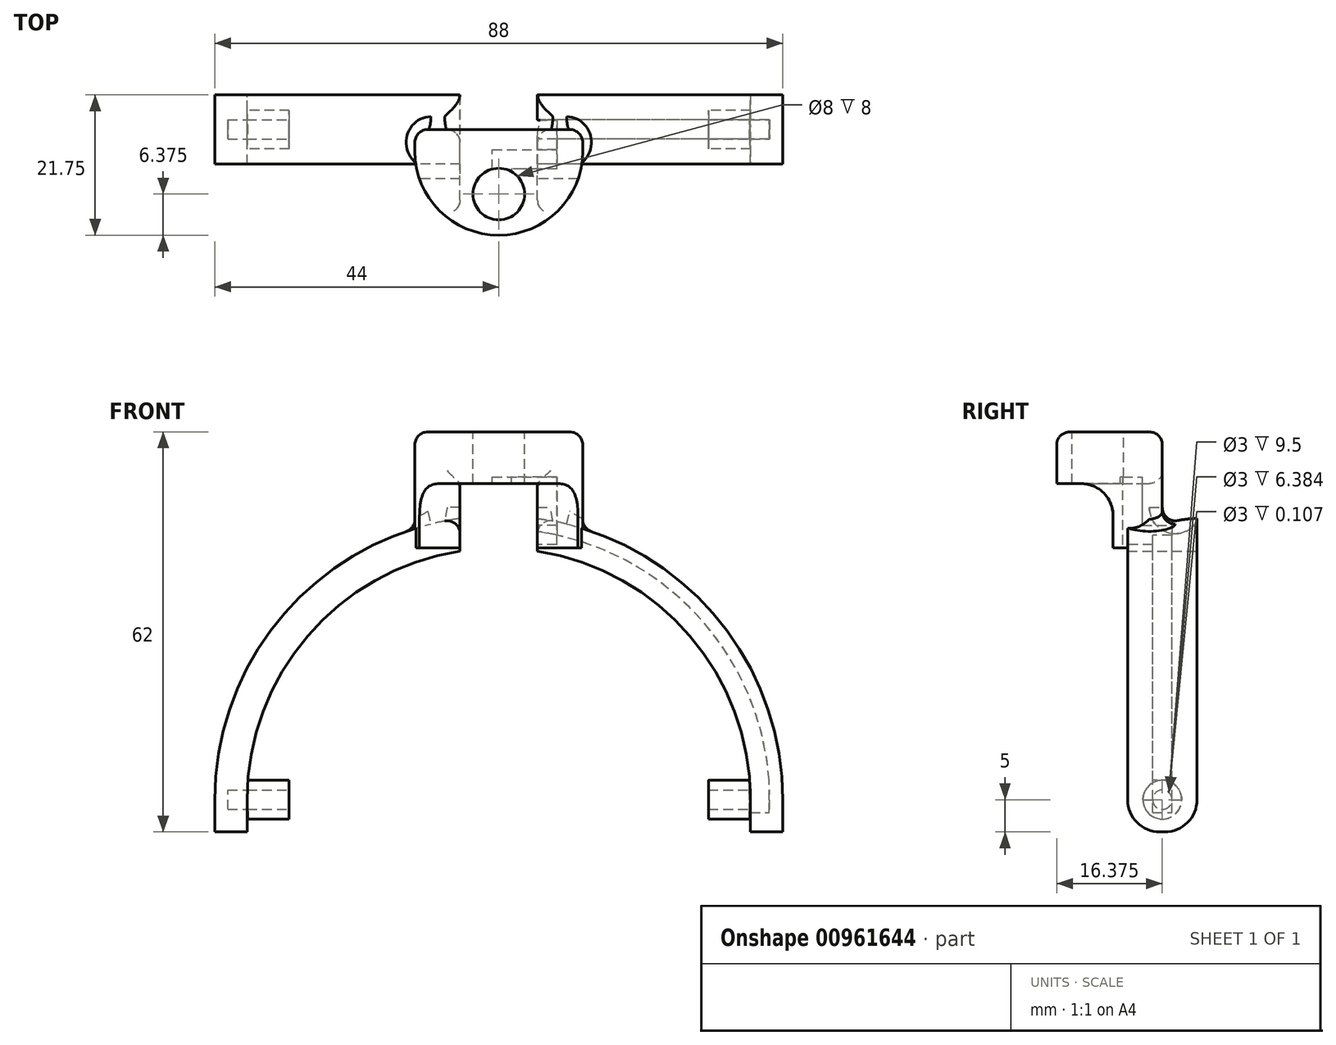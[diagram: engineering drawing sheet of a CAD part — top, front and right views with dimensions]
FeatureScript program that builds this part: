
annotation { "Feature Type Name" : "Feature", "Feature Type Description" : "" }
export const myFeature = defineFeature(function(context is Context, id is Id, definition is map)
    precondition{}
    {
        {
            var Q0;
            Q0=qCreatedBy(makeId("Front.planeOp"),FACE);
            var sketch = newSketch(context, id + "F0", { "sketchPlane" : qUnion([Q0])});
            skArc(sketch, "E0", {"start": v(39, 0) * mm, "mid": v(0, 39) * mm, "end": v(-39, 0) * mm});
            skArc(sketch, "E1", {"start": v(44, 0) * mm, "mid": v(0, 44) * mm, "end": v(-44, 0) * mm});
            skLineSegment(sketch, "E2", {"start": v(-44, 0) * mm, "end": v(-39, 0) * mm});
            skLineSegment(sketch, "E3", {"start": v(39, 0) * mm, "end": v(44, 0) * mm});
            skLineSegment(sketch, "E4", {"start": v(63.06, -5) * mm, "end": v(-58.13, -5) * mm, "construction": true});
            skLineSegment(sketch, "E5", {"start": v(44, 0) * mm, "end": v(44, -5) * mm});
            skLineSegment(sketch, "E6", {"start": v(44, -5) * mm, "end": v(39, -5) * mm});
            skLineSegment(sketch, "E7", {"start": v(39, -5) * mm, "end": v(39, 0) * mm});
            skLineSegment(sketch, "E8", {"start": v(-39, 0) * mm, "end": v(-39, -5) * mm});
            skLineSegment(sketch, "E9", {"start": v(-39, -5) * mm, "end": v(-44, -5) * mm});
            skLineSegment(sketch, "E10", {"start": v(-44, -5) * mm, "end": v(-44, 0) * mm});
            skSolve(sketch);
        }
        {
            var Q0;
            Q0=makeQuery(id+"F0.imprint","IMPRINT",FACE,{"disambiguationData":[TD([[makeQuery(id+"F0.imprint","IMPRINT",EDGE,{"derivedFrom":sQuery(id+"F0.wireOp",EDGE,"E0")}),-1.0]])]});
            var Q1;
            Q1=makeQuery(id+"F0.imprint","IMPRINT",FACE,{"disambiguationData":[TD([[makeQuery(id+"F0.imprint","IMPRINT",EDGE,{"derivedFrom":sQuery(id+"F0.wireOp",EDGE,"E3")}),-1.0]])]});
            var Q2;
            Q2=makeQuery(id+"F0.imprint","IMPRINT",FACE,{"disambiguationData":[TD([[makeQuery(id+"F0.imprint","IMPRINT",EDGE,{"derivedFrom":sQuery(id+"F0.wireOp",EDGE,"E2")}),-1.0]])]});
            extrude(context, id + "F1", {"entities" : qUnion([Q0, Q1, Q2]), "depth" : 10.75 * mm, "offsetDistance" : 25 * mm});
        }
        {
            var Q0;
            Q0=makeQuery(id+"F1.opExtrude","CAP_FACE",FACE,{"disambiguationData":[OSD([sQuery(id+"F0.wireOp",EDGE,"E0"),sQuery(id+"F0.wireOp",EDGE,"E1"),sQuery(id+"F0.wireOp",EDGE,"E2"),sQuery(id+"F0.wireOp",EDGE,"E3")])],"isStart":false});
            var sketch = newSketch(context, id + "F2", { "sketchPlane" : qUnion([Q0])});
            skLineSegment(sketch, "E11.bottom", {"start": v(-13, 57) * mm, "end": v(13, 57) * mm});
            skLineSegment(sketch, "E11.top", {"start": v(-13, 39) * mm, "end": v(13, 39) * mm});
            skLineSegment(sketch, "E11.left", {"start": v(-13, 57) * mm, "end": v(-13, 39) * mm});
            skLineSegment(sketch, "E11.right", {"start": v(13, 57) * mm, "end": v(13, 39) * mm});
            skSolve(sketch);
        }
        {
            var Q0;
            {var subQ0=sQuery(id+"F2.wireOp",EDGE,"E11.bottom");Q0=makeQuery(id+"F2.imprint","IMPRINT",FACE,{"disambiguationData":[TD([[makeQuery(id+"F2.imprint","IMPRINT",EDGE,{"derivedFrom":subQ0}),-1.0]])]});}
            var Q1;
            {var subQ0=sQuery(id+"F2.wireOp",EDGE,"E11.left");var subQ1=sQuery(id+"F2.wireOp",EDGE,"E11.top");var subQ2=makeQuery(id+"F2.imprint","INTERSECT",VERTEX,{"derivedFrom":[subQ1,subQ0]});Q1=makeQuery(id+"F2.imprint","IMPRINT",FACE,{"disambiguationData":[TD([[makeQuery(id+"F2.imprint","IMPRINT",EDGE,{"disambiguationData":[TD([[subQ2,-1.0]])],"derivedFrom":subQ1}),1.0]])]});}
            extrude(context, id + "F3", {"entities" : qUnion([Q0, Q1]), "operationType" : NewBodyOperationType.ADD, "depth" : 11 * mm, "offsetDistance" : 25 * mm, "hasSecondDirection" : true, "secondDirectionOppositeDirection" : true, "secondDirectionDepth" : 5.38 * mm});
        }
        {
            var Q0;
            Q0=qCreatedBy(makeId("Front.planeOp"),FACE);
            var sketch = newSketch(context, id + "F4", { "sketchPlane" : qUnion([Q0])});
            skLineSegment(sketch, "E12.bottom", {"start": v(-6, 32.3) * mm, "end": v(6, 32.3) * mm});
            skLineSegment(sketch, "E12.top", {"start": v(-6, 49) * mm, "end": v(6, 49) * mm});
            skLineSegment(sketch, "E12.left", {"start": v(-6, 32.3) * mm, "end": v(-6, 49) * mm});
            skLineSegment(sketch, "E12.right", {"start": v(6, 32.3) * mm, "end": v(6, 49) * mm});
            skSolve(sketch);
        }
        {
            var Q0;
            Q0=makeQuery(id+"F4.imprint","IMPRINT",FACE,{"disambiguationData":[TD([[makeQuery(id+"F4.imprint","IMPRINT",EDGE,{"derivedFrom":sQuery(id+"F4.wireOp",EDGE,"E12.bottom")}),1.0]])]});
            var Q1;
            Q1=makeQuery(id+"F3.opExtrude","CAP_FACE",FACE,{"disambiguationData":[OSD([sQuery(id+"F2.wireOp",EDGE,"E11.bottom"),sQuery(id+"F2.wireOp",EDGE,"E11.top"),sQuery(id+"F2.wireOp",EDGE,"E11.left"),sQuery(id+"F2.wireOp",EDGE,"E11.right")])],"isStart":false});
            extrude(context, id + "F5", {"entities" : qUnion([Q0]), "operationType" : NewBodyOperationType.REMOVE, "endBound" : BoundingType.UP_TO_SURFACE, "depth" : 25 * mm, "endBoundEntityFace" : qUnion([Q1]), "offsetDistance" : 25 * mm});
        }
        {
            var Q0;
            Q0=makeQuery(id+"F3.opExtrude","CAP_EDGE",EDGE,{"disambiguationData":[OSD([sQuery(id+"F2.wireOp",EDGE,"E11.right")])],"isStart":false});
            var Q1;
            Q1=makeQuery(id+"F3.opExtrude","CAP_EDGE",EDGE,{"disambiguationData":[OSD([sQuery(id+"F2.wireOp",EDGE,"E11.left")])],"isStart":false});
            fillet(context, id + "F6", {"entities" : qUnion([Q0, Q1]), "radius" : 13 * mm, "tangentPropagation" : true, "defaultsChanged" : false, "vertexSettings" : [], "allowEdgeOverflow" : false});
        }
        {
            var Q0;
            Q0=makeQuery(id+"F3.opExtrude","SWEPT_FACE",FACE,{"disambiguationData":[OSD([sQuery(id+"F2.wireOp",EDGE,"E11.bottom")])]});
            var sketch = newSketch(context, id + "F7", { "sketchPlane" : qUnion([Q0])});
            skCircle(sketch, "E13", {"center": v(0, -15.38) * mm, "radius": 4 * mm});
            skSolve(sketch);
        }
        {
            var Q0;
            Q0=makeQuery(id+"F7.imprint","IMPRINT",FACE,{"disambiguationData":[TD([[makeQuery(id+"F7.imprint","IMPRINT",EDGE,{"derivedFrom":sQuery(id+"F7.wireOp",EDGE,"E13")}),1.0]])]});
            extrude(context, id + "F8", {"entities" : qUnion([Q0]), "operationType" : NewBodyOperationType.REMOVE, "oppositeDirection" : true, "depth" : 10 * mm, "offsetDistance" : 25 * mm});
        }
        {
            var Q0;
            {var subQ0=makeQuery(id+"F1.opExtrude","SWEPT_FACE",FACE,{"disambiguationData":[OSD([sQuery(id+"F0.wireOp",EDGE,"E1")])]});var subQ1=sQuery(id+"F2.wireOp",EDGE,"E11.left");var subQ2=makeQuery(id+"F3.opExtrude","CAP_FACE",FACE,{"disambiguationData":[OSD([sQuery(id+"F2.wireOp",EDGE,"E11.bottom"),sQuery(id+"F2.wireOp",EDGE,"E11.top"),subQ1,sQuery(id+"F2.wireOp",EDGE,"E11.right")])],"isStart":true});Q0=makeQuery(id+"F5.boolean.opBoolean","SPLIT",EDGE,{"disambiguationData":[TD([makeQuery(id+"F3.opExtrude","SWEPT_FACE",FACE,{"disambiguationData":[OSD([subQ1])]})])],"derivedFrom":makeQuery(id+"F3.boolean.opBoolean","INTERSECT",EDGE,{"derivedFrom":[subQ0,subQ2]})});}
            var Q1;
            {var subQ0=makeQuery(id+"F1.opExtrude","SWEPT_FACE",FACE,{"disambiguationData":[OSD([sQuery(id+"F0.wireOp",EDGE,"E1")])]});var subQ1=sQuery(id+"F2.wireOp",EDGE,"E11.right");var subQ2=makeQuery(id+"F3.opExtrude","CAP_FACE",FACE,{"disambiguationData":[OSD([sQuery(id+"F2.wireOp",EDGE,"E11.bottom"),sQuery(id+"F2.wireOp",EDGE,"E11.top"),sQuery(id+"F2.wireOp",EDGE,"E11.left"),subQ1])],"isStart":true});Q1=makeQuery(id+"F5.boolean.opBoolean","SPLIT",EDGE,{"disambiguationData":[TD([makeQuery(id+"F3.opExtrude","SWEPT_FACE",FACE,{"disambiguationData":[OSD([subQ1])]})])],"derivedFrom":makeQuery(id+"F3.boolean.opBoolean","INTERSECT",EDGE,{"derivedFrom":[subQ0,subQ2]})});}
            var Q2;
            Q2=makeQuery(id+"F5.boolean.opBoolean","INTERSECT",EDGE,{"derivedFrom":[makeQuery(id+"F3.opExtrude","CAP_FACE",FACE,{"disambiguationData":[OSD([sQuery(id+"F2.wireOp",EDGE,"E11.bottom"),sQuery(id+"F2.wireOp",EDGE,"E11.top"),sQuery(id+"F2.wireOp",EDGE,"E11.left"),sQuery(id+"F2.wireOp",EDGE,"E11.right")])],"isStart":true}),makeQuery(id+"F5.opExtrude","SWEPT_FACE",FACE,{"disambiguationData":[OSD([sQuery(id+"F4.wireOp",EDGE,"E12.right")])]})]});
            var Q3;
            Q3=makeQuery(id+"F5.boolean.opBoolean","INTERSECT",EDGE,{"derivedFrom":[makeQuery(id+"F3.opExtrude","CAP_FACE",FACE,{"disambiguationData":[OSD([sQuery(id+"F2.wireOp",EDGE,"E11.bottom"),sQuery(id+"F2.wireOp",EDGE,"E11.top"),sQuery(id+"F2.wireOp",EDGE,"E11.left"),sQuery(id+"F2.wireOp",EDGE,"E11.right")])],"isStart":true}),makeQuery(id+"F5.opExtrude","SWEPT_FACE",FACE,{"disambiguationData":[OSD([sQuery(id+"F4.wireOp",EDGE,"E12.top")])]})]});
            var Q4;
            Q4=makeQuery(id+"F5.boolean.opBoolean","INTERSECT",EDGE,{"derivedFrom":[makeQuery(id+"F3.opExtrude","CAP_FACE",FACE,{"disambiguationData":[OSD([sQuery(id+"F2.wireOp",EDGE,"E11.bottom"),sQuery(id+"F2.wireOp",EDGE,"E11.top"),sQuery(id+"F2.wireOp",EDGE,"E11.left"),sQuery(id+"F2.wireOp",EDGE,"E11.right")])],"isStart":true}),makeQuery(id+"F5.opExtrude","SWEPT_FACE",FACE,{"disambiguationData":[OSD([sQuery(id+"F4.wireOp",EDGE,"E12.left")])]})]});
            var Q5;
            Q5=makeQuery(id+"F3.opExtrude","CAP_EDGE",EDGE,{"disambiguationData":[OSD([sQuery(id+"F2.wireOp",EDGE,"E11.left")])],"isStart":true});
            var Q6;
            Q6=makeQuery(id+"F6.opFillet","BLEND_EDGE",EDGE,{"blendedFrom":[makeQuery(id+"F3.opExtrude","CAP_EDGE",EDGE,{"disambiguationData":[OSD([sQuery(id+"F2.wireOp",EDGE,"E11.left")])],"isStart":false}),makeQuery(id+"F3.opExtrude","SWEPT_FACE",FACE,{"disambiguationData":[OSD([sQuery(id+"F2.wireOp",EDGE,"E11.bottom")])]})],"blendedInto":[makeQuery(id+"F3.opExtrude","SWEPT_FACE",FACE,{"disambiguationData":[OSD([sQuery(id+"F2.wireOp",EDGE,"E11.bottom")])]})]});
            var Q7;
            Q7=makeQuery(id+"F3.opExtrude","CAP_EDGE",EDGE,{"disambiguationData":[OSD([sQuery(id+"F2.wireOp",EDGE,"E11.bottom")])],"isStart":true});
            var Q8;
            Q8=makeQuery(id+"F3.opExtrude","CAP_EDGE",EDGE,{"disambiguationData":[OSD([sQuery(id+"F2.wireOp",EDGE,"E11.right")])],"isStart":true});
            var Q9;
            Q9=makeQuery(id+"F6.opFillet","BLEND_EDGE",EDGE,{"blendedFrom":[makeQuery(id+"F3.opExtrude","CAP_EDGE",EDGE,{"disambiguationData":[OSD([sQuery(id+"F2.wireOp",EDGE,"E11.right")])],"isStart":false}),makeQuery(id+"F5.boolean.opBoolean","COPY",FACE,{"derivedFrom":makeQuery(id+"F5.opExtrude","SWEPT_FACE",FACE,{"disambiguationData":[OSD([sQuery(id+"F4.wireOp",EDGE,"E12.top")])]})})],"blendedInto":[makeQuery(id+"F5.boolean.opBoolean","COPY",FACE,{"derivedFrom":makeQuery(id+"F5.opExtrude","SWEPT_FACE",FACE,{"disambiguationData":[OSD([sQuery(id+"F4.wireOp",EDGE,"E12.top")])]})})]});
            var Q10;
            Q10=makeQuery(id+"F6.opFillet","BLEND_EDGE",EDGE,{"blendedFrom":[makeQuery(id+"F3.opExtrude","CAP_EDGE",EDGE,{"disambiguationData":[OSD([sQuery(id+"F2.wireOp",EDGE,"E11.right")])],"isStart":false}),makeQuery(id+"F5.boolean.opBoolean","COPY",FACE,{"derivedFrom":makeQuery(id+"F5.opExtrude","SWEPT_FACE",FACE,{"disambiguationData":[OSD([sQuery(id+"F4.wireOp",EDGE,"E12.right")])]})})],"blendedInto":[makeQuery(id+"F5.boolean.opBoolean","COPY",FACE,{"derivedFrom":makeQuery(id+"F5.opExtrude","SWEPT_FACE",FACE,{"disambiguationData":[OSD([sQuery(id+"F4.wireOp",EDGE,"E12.right")])]})})]});
            var Q11;
            Q11=makeQuery(id+"F6.opFillet","BLEND_EDGE",EDGE,{"blendedFrom":[makeQuery(id+"F3.opExtrude","CAP_EDGE",EDGE,{"disambiguationData":[OSD([sQuery(id+"F2.wireOp",EDGE,"E11.left")])],"isStart":false}),makeQuery(id+"F5.boolean.opBoolean","COPY",FACE,{"derivedFrom":makeQuery(id+"F5.opExtrude","SWEPT_FACE",FACE,{"disambiguationData":[OSD([sQuery(id+"F4.wireOp",EDGE,"E12.left")])]})})],"blendedInto":[makeQuery(id+"F5.boolean.opBoolean","COPY",FACE,{"derivedFrom":makeQuery(id+"F5.opExtrude","SWEPT_FACE",FACE,{"disambiguationData":[OSD([sQuery(id+"F4.wireOp",EDGE,"E12.left")])]})})]});
            fillet(context, id + "F9", {"entities" : qUnion([Q0, Q1, Q2, Q3, Q4, Q5, Q6, Q7, Q8, Q9, Q10, Q11]), "radius" : 2 * mm, "tangentPropagation" : true, "defaultsChanged" : false, "vertexSettings" : [], "allowEdgeOverflow" : false});
        }
        {
            var Q0;
            Q0=qCreatedBy(makeId("Right.planeOp"),FACE);
            var sketch = newSketch(context, id + "F10", { "sketchPlane" : qUnion([Q0])});
            skLineSegment(sketch, "E14.bottom", {"start": v(-13, 35.02) * mm, "end": v(-25, 35.02) * mm});
            skLineSegment(sketch, "E14.top", {"start": v(-18, 49) * mm, "end": v(-25, 49) * mm});
            skLineSegment(sketch, "E14.left", {"start": v(-13, 35.02) * mm, "end": v(-13, 44) * mm});
            skLineSegment(sketch, "E14.right", {"start": v(-25, 35.02) * mm, "end": v(-25, 49) * mm});
            skPoint(sketch, "E15.visualSharp", {"position": v(-13, 49) * mm});
            skArc(sketch, "E15.filletArc", {"start": v(-13, 44) * mm, "mid": v(-14.46, 47.54) * mm, "end": v(-18, 49) * mm});
            skSolve(sketch);
        }
        {
            var Q0;
            Q0=makeQuery(id+"F10.imprint","IMPRINT",FACE,{"disambiguationData":[TD([[makeQuery(id+"F10.imprint","IMPRINT",EDGE,{"derivedFrom":sQuery(id+"F10.wireOp",EDGE,"E14.bottom")}),-1.0]])]});
            extrude(context, id + "F11", {"entities" : qUnion([Q0]), "operationType" : NewBodyOperationType.REMOVE, "oppositeDirection" : true, "depth" : 25 * mm, "offsetDistance" : 25 * mm, "hasSecondDirection" : true, "secondDirectionOppositeDirection" : false, "secondDirectionDepth" : 25 * mm});
        }
        {
            var Q0;
            Q0=qCreatedBy(makeId("Right.planeOp"),FACE);
            var sketch = newSketch(context, id + "F12", { "sketchPlane" : qUnion([Q0])});
            skCircle(sketch, "E16", {"center": v(-5.38, 0) * mm, "radius": 3 * mm});
            skSolve(sketch);
        }
        {
            var Q0;
            Q0=makeQuery(id+"F12.imprint","IMPRINT",FACE,{"disambiguationData":[TD([[makeQuery(id+"F12.imprint","IMPRINT",EDGE,{"derivedFrom":sQuery(id+"F12.wireOp",EDGE,"E16")}),1.0]])]});
            var Q1;
            {var subQ2=sQuery(id+"F0.wireOp",EDGE,"E8");var subQ7=sQuery(id+"F0.wireOp",EDGE,"E0");Q1=makeQuery(id+"F5.boolean.opBoolean","SPLIT",FACE,{"disambiguationData":[TD([makeQuery(id+"F1.opExtrude","SWEPT_FACE",FACE,{"disambiguationData":[OSD([subQ2])]})])],"derivedFrom":makeQuery(id+"F1.opExtrude","SWEPT_FACE",FACE,{"disambiguationData":[OSD([subQ7])]})});}
            var Q2;
            {var subQ2=sQuery(id+"F0.wireOp",EDGE,"E8");var subQ7=sQuery(id+"F0.wireOp",EDGE,"E0");Q2=makeQuery(id+"F5.boolean.opBoolean","SPLIT",FACE,{"disambiguationData":[TD([makeQuery(id+"F1.opExtrude","SWEPT_FACE",FACE,{"disambiguationData":[OSD([subQ2])]})])],"derivedFrom":makeQuery(id+"F1.opExtrude","SWEPT_FACE",FACE,{"disambiguationData":[OSD([subQ7])]})});}
            extrude(context, id + "F13", {"entities" : qUnion([Q0]), "operationType" : NewBodyOperationType.ADD, "endBound" : BoundingType.UP_TO_SURFACE, "depth" : 25 * mm, "endBoundEntityFace" : qUnion([Q1]), "offsetDistance" : 25 * mm, "hasSecondDirection" : true, "secondDirectionBound" : SecondDirectionBoundingType.UP_TO_SURFACE, "secondDirectionOppositeDirection" : true, "secondDirectionDepth" : 25 * mm, "secondDirectionBoundEntityFace" : qUnion([Q2])});
        }
        {
            var Q0;
            Q0=qCreatedBy(makeId("Front.planeOp"),FACE);
            var sketch = newSketch(context, id + "F14", { "sketchPlane" : qUnion([Q0])});
            skLineSegment(sketch, "E17.bottom", {"start": v(-32.5, 7) * mm, "end": v(32.5, 7) * mm});
            skLineSegment(sketch, "E17.top", {"start": v(-32.5, -8) * mm, "end": v(32.5, -8) * mm});
            skLineSegment(sketch, "E17.left", {"start": v(-32.5, 7) * mm, "end": v(-32.5, -8) * mm});
            skLineSegment(sketch, "E17.right", {"start": v(32.5, 7) * mm, "end": v(32.5, -8) * mm});
            skSolve(sketch);
        }
        {
            var Q0;
            Q0=makeQuery(id+"F14.imprint","IMPRINT",FACE,{"disambiguationData":[TD([[makeQuery(id+"F14.imprint","IMPRINT",EDGE,{"derivedFrom":sQuery(id+"F14.wireOp",EDGE,"E17.bottom")}),-1.0]])]});
            extrude(context, id + "F15", {"entities" : qUnion([Q0]), "operationType" : NewBodyOperationType.REMOVE, "depth" : 10 * mm, "offsetDistance" : 25 * mm});
        }
        {
            var Q0;
            Q0=makeQuery(id+"F1.opExtrude","CAP_EDGE",EDGE,{"disambiguationData":[OSD([sQuery(id+"F0.wireOp",EDGE,"E9")])],"isStart":false});
            var Q1;
            Q1=makeQuery(id+"F1.opExtrude","CAP_EDGE",EDGE,{"disambiguationData":[OSD([sQuery(id+"F0.wireOp",EDGE,"E9")])],"isStart":true});
            var Q2;
            Q2=makeQuery(id+"F1.opExtrude","CAP_EDGE",EDGE,{"disambiguationData":[OSD([sQuery(id+"F0.wireOp",EDGE,"E6")])],"isStart":false});
            var Q3;
            Q3=makeQuery(id+"F1.opExtrude","CAP_EDGE",EDGE,{"disambiguationData":[OSD([sQuery(id+"F0.wireOp",EDGE,"E6")])],"isStart":true});
            fillet(context, id + "F16", {"entities" : qUnion([Q0, Q1, Q2, Q3]), "tangentPropagation" : true, "radius" : 5 * mm, "defaultsChanged" : false, "vertexSettings" : [], "allowEdgeOverflow" : false});
        }
        {
            var Q0;
            Q0=makeQuery(id+"F5.boolean.opBoolean","COPY",FACE,{"derivedFrom":makeQuery(id+"F5.opExtrude","SWEPT_FACE",FACE,{"disambiguationData":[OSD([sQuery(id+"F4.wireOp",EDGE,"E12.right")])]})});
            var sketch = newSketch(context, id + "F17", { "sketchPlane" : qUnion([Q0])});
            skLineSegment(sketch, "E18", {"start": v(6.8, 39.04) * mm, "end": v(6.8, 39.54) * mm});
            skLineSegment(sketch, "E19", {"start": v(6.8, 39.54) * mm, "end": v(11.51, 39.54) * mm});
            skLineSegment(sketch, "E20", {"start": v(11.51, 39.54) * mm, "end": v(11.51, 49) * mm});
            skLineSegment(sketch, "E21", {"start": v(8.51, 49) * mm, "end": v(8.51, 42.54) * mm});
            skLineSegment(sketch, "E22", {"start": v(8.51, 42.54) * mm, "end": v(3.9, 42.54) * mm});
            skLineSegment(sketch, "E23", {"start": v(3.9, 42.54) * mm, "end": v(3.9, 39.53) * mm});
            skLineSegment(sketch, "E24", {"start": v(3.9, 39.53) * mm, "end": v(6.8, 39.54) * mm});
            skLineSegment(sketch, "E25", {"start": v(8.51, 49) * mm, "end": v(11.51, 49) * mm});
            skLineSegment(sketch, "E26", {"start": v(3.9, 39.53) * mm, "end": v(3.9, 39.03) * mm});
            skLineSegment(sketch, "E27", {"start": v(3.9, 39.03) * mm, "end": v(6.8, 39.04) * mm});
            skSolve(sketch);
        }
        {
            var Q0;
            {var subQ13=sQuery(id+"F17.wireOp",EDGE,"E19");Q0=makeQuery(id+"F17.imprint","IMPRINT",FACE,{"disambiguationData":[TD([[makeQuery(id+"F17.imprint","IMPRINT",EDGE,{"derivedFrom":subQ13}),1.0]])]});}
            var Q1;
            {var subQ0=sQuery(id+"F17.wireOp",EDGE,"E23");var subQ1=sQuery(id+"F17.wireOp",EDGE,"E22");var subQ2=makeQuery(id+"F17.imprint","INTERSECT",VERTEX,{"derivedFrom":[subQ1,subQ0]});Q1=makeQuery(id+"F17.imprint","IMPRINT",FACE,{"disambiguationData":[TD([[makeQuery(id+"F17.imprint","IMPRINT",EDGE,{"disambiguationData":[TD([[subQ2,-1.0]])],"derivedFrom":subQ0}),1.0]])]});}
            var Q2;
            {var subQ13=sQuery(id+"F17.wireOp",EDGE,"E24");Q2=makeQuery(id+"F17.imprint","IMPRINT",FACE,{"disambiguationData":[TD([[makeQuery(id+"F17.imprint","IMPRINT",EDGE,{"derivedFrom":subQ13}),-1.0]])]});}
            extrude(context, id + "F18", {"entities" : qUnion([Q0, Q1, Q2]), "operationType" : NewBodyOperationType.REMOVE, "oppositeDirection" : true, "depth" : 3 * mm, "offsetDistance" : 25 * mm});
        }
        {
            var Q0;
            Q0=makeQuery(id+"F18.boolean.opBoolean","MERGE",FACE,{"derivedFrom":[makeQuery(id+"F11.boolean.opBoolean","MERGE",FACE,{"derivedFrom":[makeQuery(id+"F5.boolean.opBoolean","COPY",FACE,{"derivedFrom":makeQuery(id+"F5.opExtrude","SWEPT_FACE",FACE,{"disambiguationData":[OSD([sQuery(id+"F4.wireOp",EDGE,"E12.top")])]})})],"fromTools":[makeQuery(id+"F11.opExtrude","SWEPT_FACE",FACE,{"disambiguationData":[OSD([sQuery(id+"F10.wireOp",EDGE,"E14.top")])]})]})],"fromTools":[makeQuery(id+"F18.opExtrude","SWEPT_FACE",FACE,{"disambiguationData":[OSD([sQuery(id+"F17.wireOp",EDGE,"E25")])]})]});
            var sketch = newSketch(context, id + "F19", { "sketchPlane" : qUnion([Q0])});
            skSolve(sketch);
        }
        {
            var Q0;
            {var subQ25=sQuery(id+"F17.wireOp",EDGE,"E25");Q0=makeQuery(id+"F19.imprint","IMPRINT",FACE,{"disambiguationData":[TD([[makeQuery(id+"F19.imprint","IMPRINT",EDGE,{"derivedFrom":makeQuery(id+"F18.boolean.opBoolean","COPY",EDGE,{"derivedFrom":makeQuery(id+"F18.opExtrude","CAP_EDGE",EDGE,{"disambiguationData":[OSD([subQ25])],"isStart":false})})}),-1.0]])]});}
            var sketch = newSketch(context, id + "F20", { "sketchPlane" : qUnion([Q0])});
            skLineSegment(sketch, "E28", {"start": v(9, 11.51) * mm, "end": v(2, 11.51) * mm});
            skLineSegment(sketch, "E29", {"start": v(2, 11.51) * mm, "end": v(2, 13.51) * mm});
            skLineSegment(sketch, "E30", {"start": v(2, 13.51) * mm, "end": v(-1, 13.51) * mm});
            skLineSegment(sketch, "E31", {"start": v(-1, 13.51) * mm, "end": v(-1, 8.51) * mm});
            skLineSegment(sketch, "E32", {"start": v(-1, 8.51) * mm, "end": v(9, 8.51) * mm});
            skLineSegment(sketch, "E33", {"start": v(9, 8.51) * mm, "end": v(9, 11.51) * mm});
            skSolve(sketch);
        }
        {
            var Q0;
            Q0 = qSketchRegion(id + "F20", true);
            extrude(context, id + "F21", {"entities" : qUnion([Q0]), "operationType" : NewBodyOperationType.REMOVE, "oppositeDirection" : true, "depth" : 1 * mm, "offsetDistance" : 25 * mm});
        }
        {
            var Q0;
            Q0=qCreatedBy(makeId("Front.planeOp"),FACE);
            cPlane(context, id + "F22", {"entities" : qUnion([Q0]), "cplaneType" : CPlaneType.OFFSET, "offset" : (10.75 / 2) * mm, "width" : 150 * mm, "height" : 150 * mm});
        }
        {
            var Q0;
            Q0=qCreatedBy(id+"F22.planeOp",FACE);
            var sketch = newSketch(context, id + "F23", { "sketchPlane" : qUnion([Q0])});
            skArc(sketch, "E34", {"start": v(38.88, 3) * mm, "mid": v(26.5, 28.62) * mm, "end": v(0, 39) * mm});
            skArc(sketch, "E35", {"start": v(41.9, 3) * mm, "mid": v(28.62, 30.74) * mm, "end": v(0, 42) * mm});
            skLineSegment(sketch, "E36", {"start": v(-38.88, 3) * mm, "end": v(80.6, 3) * mm, "construction": true});
            skLineSegment(sketch, "E37", {"start": v(38.88, 3) * mm, "end": v(41.9, 3) * mm});
            skLineSegment(sketch, "E38", {"start": v(0, 39) * mm, "end": v(0, 42) * mm});
            skLineSegment(sketch, "E39", {"start": v(0, -17.93) * mm, "end": v(0, 68.95) * mm, "construction": true});
            skSolve(sketch);
        }
        {
            var Q0;
            Q0=makeQuery(id+"F23.imprint","IMPRINT",FACE,{"disambiguationData":[TD([[makeQuery(id+"F23.imprint","IMPRINT",EDGE,{"derivedFrom":sQuery(id+"F23.wireOp",EDGE,"E34")}),-1.0]])]});
            extrude(context, id + "F24", {"entities" : qUnion([Q0]), "operationType" : NewBodyOperationType.REMOVE, "oppositeDirection" : true, "depth" : 1.5 * mm, "offsetDistance" : 25 * mm, "hasSecondDirection" : true, "secondDirectionOppositeDirection" : false, "secondDirectionDepth" : 1.5 * mm});
        }
        {
            var Q0;
            Q0=qCreatedBy(makeId("Right.planeOp"),FACE);
            var sketch = newSketch(context, id + "F25", { "sketchPlane" : qUnion([Q0])});
            skCircle(sketch, "E40", {"center": v(-5.38, 0) * mm, "radius": 1.5 * mm});
            skSolve(sketch);
        }
        {
            var Q0;
            Q0=makeQuery(id+"F25.imprint","IMPRINT",FACE,{"disambiguationData":[TD([[makeQuery(id+"F25.imprint","IMPRINT",EDGE,{"derivedFrom":sQuery(id+"F25.wireOp",EDGE,"E40")}),1.0]])]});
            extrude(context, id + "F26", {"entities" : qUnion([Q0]), "operationType" : NewBodyOperationType.REMOVE, "oppositeDirection" : true, "depth" : 42 * mm, "offsetDistance" : 25 * mm, "hasSecondDirection" : true, "secondDirectionOppositeDirection" : false, "secondDirectionDepth" : 42 * mm});
        }
        {
            var Q0;
            Q0=makeQuery(id+"F24.boolean.opBoolean","COPY",FACE,{"derivedFrom":makeQuery(id+"F24.opExtrude","SWEPT_FACE",FACE,{"disambiguationData":[OSD([sQuery(id+"F23.wireOp",EDGE,"E37")])]})});
            var sketch = newSketch(context, id + "F27", { "sketchPlane" : qUnion([Q0])});
            skLineSegment(sketch, "E41.bottom", {"start": v(38.88, -3.88) * mm, "end": v(41.9, -3.88) * mm});
            skLineSegment(sketch, "E41.top", {"start": v(38.88, -6.88) * mm, "end": v(41.9, -6.88) * mm});
            skLineSegment(sketch, "E41.left", {"start": v(38.88, -3.88) * mm, "end": v(38.88, -6.88) * mm});
            skLineSegment(sketch, "E41.right", {"start": v(41.9, -3.88) * mm, "end": v(41.9, -6.88) * mm});
            skSolve(sketch);
        }
        {
            var Q0;
            Q0 = qSketchRegion(id + "F27", true);
            extrude(context, id + "F28", {"entities" : qUnion([Q0]), "operationType" : NewBodyOperationType.REMOVE, "oppositeDirection" : true, "depth" : 5 * mm, "offsetDistance" : 25 * mm});
        }
    });
